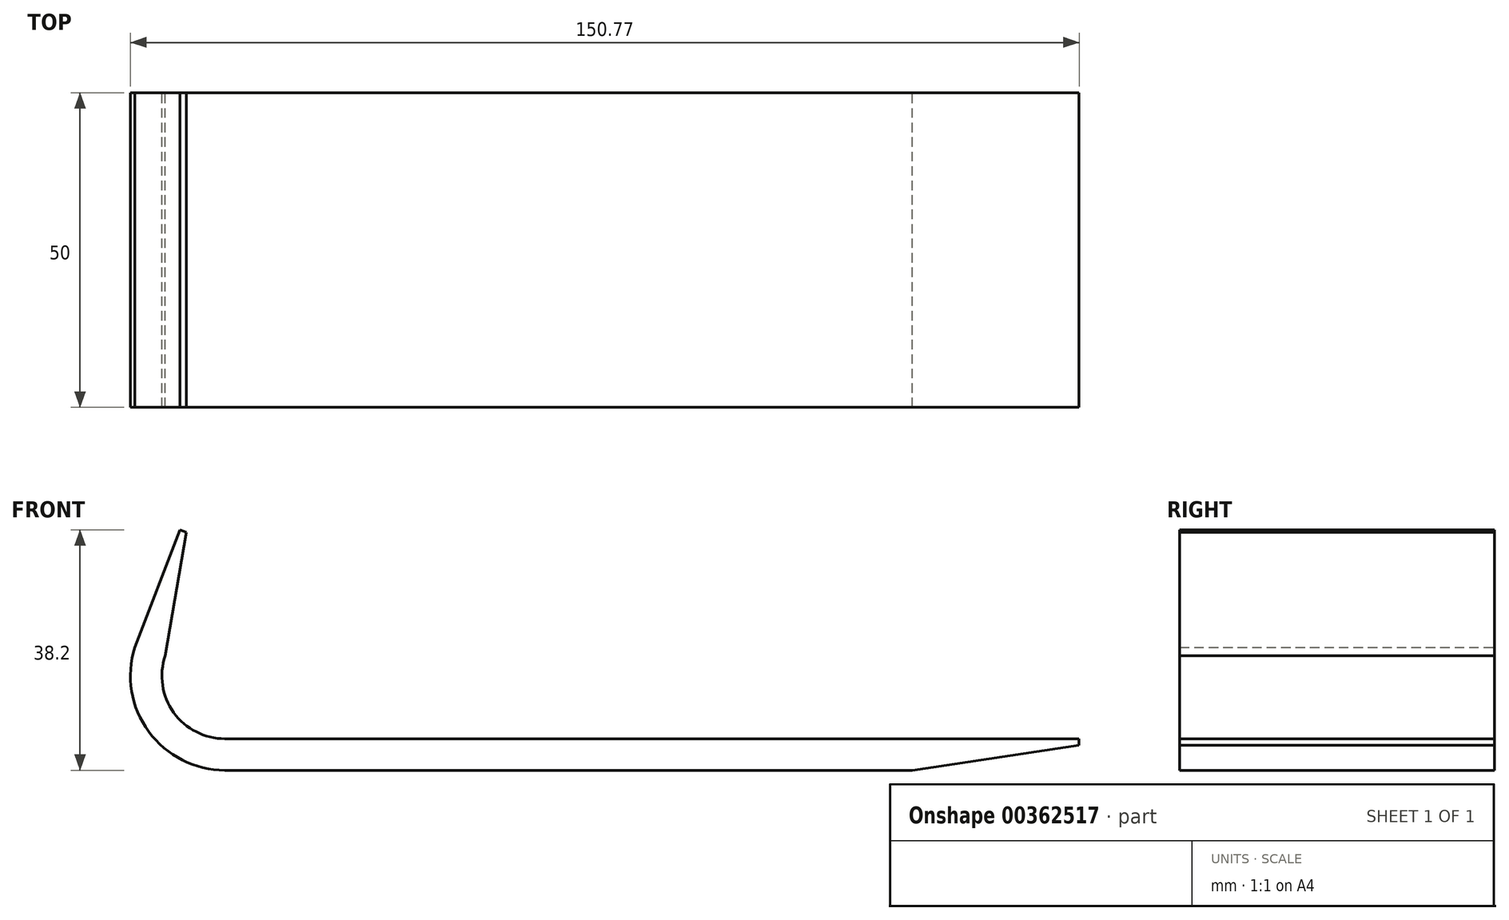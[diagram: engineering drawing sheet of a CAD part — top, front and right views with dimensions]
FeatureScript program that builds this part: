
annotation { "Feature Type Name" : "Feature", "Feature Type Description" : "" }
export const myFeature = defineFeature(function(context is Context, id is Id, definition is map)
    precondition{}
    {
        {
            var Q0;
            Q0=qCreatedBy(makeId("Front.planeOp"),FACE);
            var sketch = newSketch(context, id + "F0", { "sketchPlane" : qUnion([Q0])});
            skLineSegment(sketch, "E0", {"start": v(75, 0) * mm, "end": v(-75, 0) * mm, "construction": true});
            skCircle(sketch, "E1", {"center": v(-60.77, 15) * mm, "radius": 15 * mm, "construction": true});
            skCircle(sketch, "E2", {"center": v(-60.77, 15) * mm, "radius": 10 * mm, "construction": true});
            skLineSegment(sketch, "E3", {"start": v(-75.07, 19.52) * mm, "end": v(-67.9, 38.2) * mm, "construction": true});
            skLineSegment(sketch, "E4", {"start": v(-67.9, 38.2) * mm, "end": v(-66.87, 37.8) * mm, "construction": true});
            skLineSegment(sketch, "E5", {"start": v(-66.87, 37.8) * mm, "end": v(-70.25, 18.2) * mm, "construction": true});
            skArc(sketch, "E6", {"start": v(-60.77, 5) * mm, "mid": v(-68.9, 9.17) * mm, "end": v(-70.25, 18.2) * mm});
            skArc(sketch, "E7", {"start": v(-60.77, 0) * mm, "mid": v(-72.87, 6.14) * mm, "end": v(-75.07, 19.52) * mm});
            skLineSegment(sketch, "E8", {"start": v(-75.07, 19.52) * mm, "end": v(-67.9, 38.2) * mm});
            skLineSegment(sketch, "E9", {"start": v(-66.87, 37.8) * mm, "end": v(-70.25, 18.2) * mm});
            skLineSegment(sketch, "E10", {"start": v(-60.77, 5) * mm, "end": v(75, 5) * mm});
            skLineSegment(sketch, "E11", {"start": v(75, 5) * mm, "end": v(75, 3.97) * mm});
            skLineSegment(sketch, "E12", {"start": v(75, 3.97) * mm, "end": v(48.5, 0) * mm});
            skLineSegment(sketch, "E13", {"start": v(-60.77, 0) * mm, "end": v(48.5, 0) * mm});
            skLineSegment(sketch, "E14", {"start": v(-67.9, 38.2) * mm, "end": v(-66.87, 37.8) * mm});
            skSolve(sketch);
        }
        {
            var Q0;
            Q0 = qSketchRegion(id + "F0", true);
            extrude(context, id + "F1", {"entities" : qUnion([Q0]), "depth" : 50 * mm});
        }
    });
